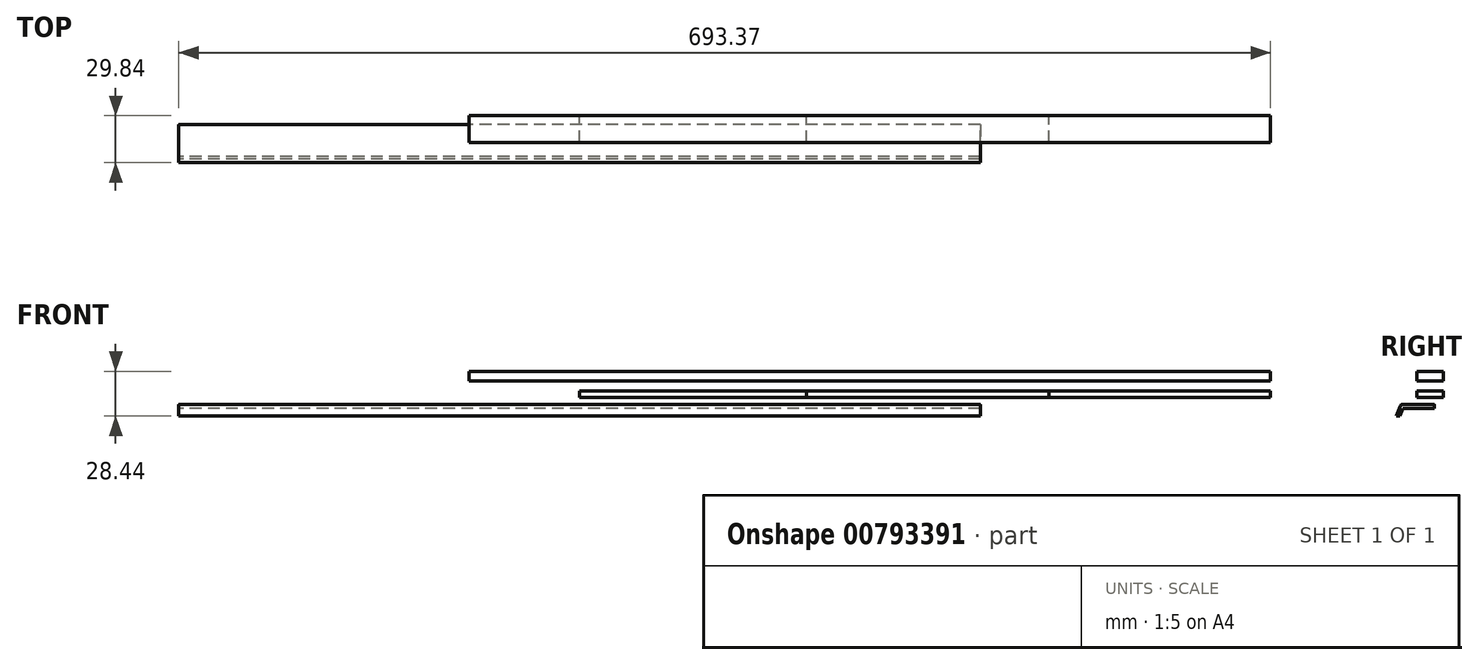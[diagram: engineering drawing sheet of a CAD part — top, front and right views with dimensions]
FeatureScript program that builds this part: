
annotation { "Feature Type Name" : "Feature", "Feature Type Description" : "" }
export const myFeature = defineFeature(function(context is Context, id is Id, definition is map)
    precondition{}
    {
        {
            var Q0;
            Q0=qCreatedBy(makeId("Right.planeOp"),FACE);
            var sketch = newSketch(context, id + "F0", { "sketchPlane" : qUnion([Q0])});
            skLineSegment(sketch, "E0", {"start": v(-242.05, -0.45) * mm, "end": v(-221.91, -0.45) * mm});
            skLineSegment(sketch, "E1", {"start": v(-221.61, -0.75) * mm, "end": v(-221.61, -3.05) * mm});
            skLineSegment(sketch, "E2", {"start": v(-221.61, -3.05) * mm, "end": v(-241.81, -3.05) * mm});
            skLineSegment(sketch, "E3", {"start": v(-241.81, -3.05) * mm, "end": v(-243.56, -7.83) * mm});
            skLineSegment(sketch, "E4", {"start": v(-243.56, -7.83) * mm, "end": v(-245.8, -7.83) * mm});
            skLineSegment(sketch, "E5", {"start": v(-245.8, -7.83) * mm, "end": v(-243.46, -1.44) * mm});
            skPoint(sketch, "E6.visualSharp", {"position": v(-243.1, -0.45) * mm});
            skArc(sketch, "E6.filletArc", {"start": v(-242.05, -0.45) * mm, "mid": v(-242.9, -0.72) * mm, "end": v(-243.46, -1.44) * mm});
            skPoint(sketch, "E7.visualSharp", {"position": v(-221.61, -0.45) * mm});
            skArc(sketch, "E7.filletArc", {"start": v(-221.61, -0.75) * mm, "mid": v(-221.7, -0.54) * mm, "end": v(-221.91, -0.45) * mm});
            skSolve(sketch);
        }
        {
            var Q0;
            Q0=makeQuery(id+"F0.imprint","IMPRINT",FACE,{"disambiguationData":[TD([[makeQuery(id+"F0.imprint","IMPRINT",EDGE,{"derivedFrom":sQuery(id+"F0.wireOp",EDGE,"E0")}),-1.0]])]});
            extrude(context, id + "F1", {"entities" : qUnion([Q0]), "depth" : 509 * mm, "offsetDistance" : 25 * mm, "symmetric" : true});
        }
        {
            var Q0;
            Q0=qCreatedBy(makeId("Right.planeOp"),FACE);
            var sketch = newSketch(context, id + "F2", { "sketchPlane" : qUnion([Q0])});
            skLineSegment(sketch, "E8.bottom", {"start": v(-232.9, 8.1) * mm, "end": v(-215.95, 8.1) * mm});
            skLineSegment(sketch, "E8.top", {"start": v(-232.9, 4.1) * mm, "end": v(-215.95, 4.1) * mm});
            skLineSegment(sketch, "E8.left", {"start": v(-232.9, 8.1) * mm, "end": v(-232.9, 4.1) * mm});
            skLineSegment(sketch, "E8.right", {"start": v(-215.95, 8.1) * mm, "end": v(-215.95, 4.1) * mm});
            skSolve(sketch);
        }
        {
            var Q0;
            Q0=makeQuery(id+"F2.imprint","IMPRINT",FACE,{"disambiguationData":[TD([[makeQuery(id+"F2.imprint","IMPRINT",EDGE,{"derivedFrom":sQuery(id+"F2.wireOp",EDGE,"E8.bottom")}),-1.0]])]});
            extrude(context, id + "F3", {"entities" : qUnion([Q0]), "depth" : 144.1 * mm, "offsetDistance" : 25 * mm});
        }
        {
            var Q0;
            Q0=makeQuery(id+"F3.opExtrude","CAP_FACE",FACE,{"disambiguationData":[OSD([sQuery(id+"F2.wireOp",EDGE,"E8.bottom"),sQuery(id+"F2.wireOp",EDGE,"E8.top"),sQuery(id+"F2.wireOp",EDGE,"E8.left"),sQuery(id+"F2.wireOp",EDGE,"E8.right")])],"isStart":false});
            extrude(context, id + "F4", {"entities" : qUnion([Q0]), "depth" : 154.11 * mm, "offsetDistance" : 25 * mm});
        }
        {
            var Q0;
            Q0=makeQuery(id+"F4.opExtrude","CAP_FACE",FACE,{"disambiguationData":[OSD([sQuery(id+"F2.wireOp",EDGE,"E8.bottom"),sQuery(id+"F2.wireOp",EDGE,"E8.top"),sQuery(id+"F2.wireOp",EDGE,"E8.left"),sQuery(id+"F2.wireOp",EDGE,"E8.right")])],"isStart":false});
            extrude(context, id + "F5", {"entities" : qUnion([Q0]), "depth" : 140.67 * mm, "offsetDistance" : 25 * mm});
        }
        {
            var Q0;
            Q0=makeQuery(id+"F5.opExtrude","CAP_FACE",FACE,{"disambiguationData":[OSD([sQuery(id+"F2.wireOp",EDGE,"E8.bottom"),sQuery(id+"F2.wireOp",EDGE,"E8.top"),sQuery(id+"F2.wireOp",EDGE,"E8.left"),sQuery(id+"F2.wireOp",EDGE,"E8.right")])],"isStart":false});
            var sketch = newSketch(context, id + "F6", { "sketchPlane" : qUnion([Q0])});
            skLineSegment(sketch, "E9.bottom", {"start": v(-232.9, 14.6) * mm, "end": v(-215.95, 14.6) * mm});
            skLineSegment(sketch, "E9.top", {"start": v(-232.9, 20.6) * mm, "end": v(-215.95, 20.6) * mm});
            skLineSegment(sketch, "E9.left", {"start": v(-232.9, 14.6) * mm, "end": v(-232.9, 20.6) * mm});
            skLineSegment(sketch, "E9.right", {"start": v(-215.95, 14.6) * mm, "end": v(-215.95, 20.6) * mm});
            skSolve(sketch);
        }
        {
            var Q0;
            Q0=makeQuery(id+"F6.imprint","IMPRINT",FACE,{"disambiguationData":[TD([[makeQuery(id+"F6.imprint","IMPRINT",EDGE,{"derivedFrom":sQuery(id+"F6.wireOp",EDGE,"E9.bottom")}),1.0]])]});
            extrude(context, id + "F7", {"entities" : qUnion([Q0]), "oppositeDirection" : true, "depth" : 509 * mm, "offsetDistance" : 25 * mm});
        }
    });
